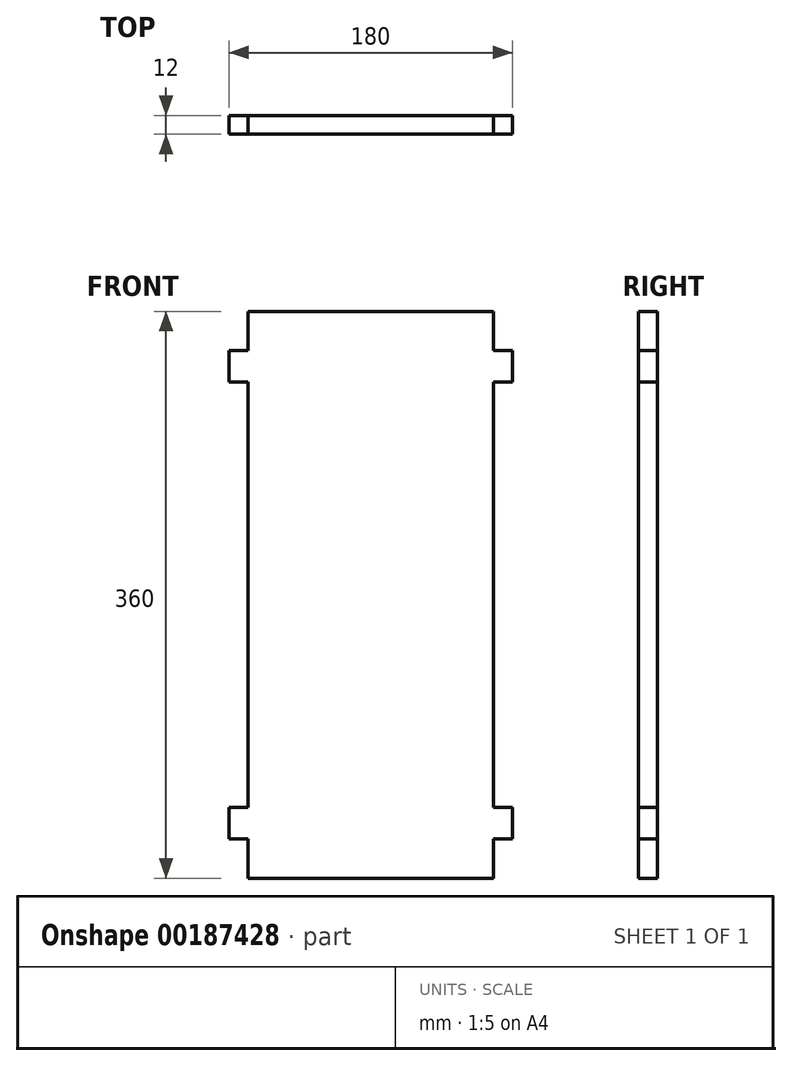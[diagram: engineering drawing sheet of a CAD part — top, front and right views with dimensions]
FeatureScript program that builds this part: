
annotation { "Feature Type Name" : "Feature", "Feature Type Description" : "" }
export const myFeature = defineFeature(function(context is Context, id is Id, definition is map)
    precondition{}
    {
        {
            var Q0;
            Q0=qCreatedBy(makeId("Front.planeOp"),FACE);
            var sketch = newSketch(context, id + "F0", { "sketchPlane" : qUnion([Q0])});
            skLineSegment(sketch, "E0.bottom", {"start": v(90, 180) * mm, "end": v(-90, 180) * mm});
            skLineSegment(sketch, "E0.top", {"start": v(90, -180) * mm, "end": v(-90, -180) * mm});
            skLineSegment(sketch, "E0.left", {"start": v(90, 180) * mm, "end": v(90, -180) * mm});
            skLineSegment(sketch, "E0.right", {"start": v(-90, 180) * mm, "end": v(-90, -180) * mm});
            skPoint(sketch, "E0.middle", {"position": v(0, 0) * mm});
            skLineSegment(sketch, "E1.bottom", {"start": v(-78, -135) * mm, "end": v(-102, -135) * mm});
            skLineSegment(sketch, "E1.top", {"start": v(-78, -155) * mm, "end": v(-102, -155) * mm});
            skLineSegment(sketch, "E1.left", {"start": v(-78, -135) * mm, "end": v(-78, -155) * mm});
            skLineSegment(sketch, "E1.right", {"start": v(-102, -135) * mm, "end": v(-102, -155) * mm});
            skPoint(sketch, "E1.middle", {"position": v(-90, -145) * mm});
            skLineSegment(sketch, "E2.MirrorCS", {"start": v(102, -135) * mm, "end": v(102, -155) * mm});
            skLineSegment(sketch, "E3.MirrorCS", {"start": v(78, -135) * mm, "end": v(102, -135) * mm});
            skLineSegment(sketch, "E4.MirrorCS", {"start": v(78, -155) * mm, "end": v(102, -155) * mm});
            skLineSegment(sketch, "E5.MirrorCS", {"start": v(78, -135) * mm, "end": v(78, -155) * mm});
            skPoint(sketch, "E6.MirrorP", {"position": v(90, -145) * mm});
            skLineSegment(sketch, "E7.bottom", {"start": v(-78, 155) * mm, "end": v(-102, 155) * mm});
            skLineSegment(sketch, "E7.top", {"start": v(-78, 135) * mm, "end": v(-102, 135) * mm});
            skLineSegment(sketch, "E7.left", {"start": v(-78, 155) * mm, "end": v(-78, 135) * mm});
            skLineSegment(sketch, "E7.right", {"start": v(-102, 155) * mm, "end": v(-102, 135) * mm});
            skPoint(sketch, "E7.middle", {"position": v(-90, 145) * mm});
            skLineSegment(sketch, "E8.MirrorCS", {"start": v(102, 155) * mm, "end": v(102, 135) * mm});
            skLineSegment(sketch, "E9.MirrorCS", {"start": v(78, 155) * mm, "end": v(102, 155) * mm});
            skLineSegment(sketch, "E10.MirrorCS", {"start": v(78, 155) * mm, "end": v(78, 135) * mm});
            skLineSegment(sketch, "E11.MirrorCS", {"start": v(78, 135) * mm, "end": v(102, 135) * mm});
            skPoint(sketch, "E12.MirrorP", {"position": v(90, 145) * mm});
            skSolve(sketch);
        }
        {
            var Q0;
            {var subQ5=sQuery(id+"F0.wireOp",EDGE,"E7.right");Q0=makeQuery(id+"F0.imprint","IMPRINT",FACE,{"disambiguationData":[TD([[makeQuery(id+"F0.imprint","IMPRINT",EDGE,{"derivedFrom":subQ5}),1.0]])]});}
            var Q1;
            {var subQ5=sQuery(id+"F0.wireOp",EDGE,"E1.right");Q1=makeQuery(id+"F0.imprint","IMPRINT",FACE,{"disambiguationData":[TD([[makeQuery(id+"F0.imprint","IMPRINT",EDGE,{"derivedFrom":subQ5}),1.0]])]});}
            var Q2;
            {var subQ0=sQuery(id+"F0.wireOp",EDGE,"E2.MirrorCS");Q2=makeQuery(id+"F0.imprint","IMPRINT",FACE,{"disambiguationData":[TD([[makeQuery(id+"F0.imprint","IMPRINT",EDGE,{"derivedFrom":subQ0}),-1.0]])]});}
            var Q3;
            {var subQ5=sQuery(id+"F0.wireOp",EDGE,"E8.MirrorCS");Q3=makeQuery(id+"F0.imprint","IMPRINT",FACE,{"disambiguationData":[TD([[makeQuery(id+"F0.imprint","IMPRINT",EDGE,{"derivedFrom":subQ5}),-1.0]])]});}
            var Q4;
            {var subQ5=sQuery(id+"F0.wireOp",EDGE,"E7.left");Q4=makeQuery(id+"F0.imprint","IMPRINT",FACE,{"disambiguationData":[TD([[makeQuery(id+"F0.imprint","IMPRINT",EDGE,{"derivedFrom":subQ5}),-1.0]])]});}
            var Q5;
            {var subQ5=sQuery(id+"F0.wireOp",EDGE,"E1.left");Q5=makeQuery(id+"F0.imprint","IMPRINT",FACE,{"disambiguationData":[TD([[makeQuery(id+"F0.imprint","IMPRINT",EDGE,{"derivedFrom":subQ5}),-1.0]])]});}
            var Q6;
            {var subQ0=sQuery(id+"F0.wireOp",EDGE,"E5.MirrorCS");Q6=makeQuery(id+"F0.imprint","IMPRINT",FACE,{"disambiguationData":[TD([[makeQuery(id+"F0.imprint","IMPRINT",EDGE,{"derivedFrom":subQ0}),1.0]])]});}
            var Q7;
            {var subQ5=sQuery(id+"F0.wireOp",EDGE,"E10.MirrorCS");Q7=makeQuery(id+"F0.imprint","IMPRINT",FACE,{"disambiguationData":[TD([[makeQuery(id+"F0.imprint","IMPRINT",EDGE,{"derivedFrom":subQ5}),1.0]])]});}
            var Q8;
            {var subQ17=sQuery(id+"F0.wireOp",EDGE,"E0.bottom");Q8=makeQuery(id+"F0.imprint","IMPRINT",FACE,{"disambiguationData":[TD([[makeQuery(id+"F0.imprint","IMPRINT",EDGE,{"derivedFrom":subQ17}),1.0]])]});}
            extrude(context, id + "F1", {"entities" : qUnion([Q0, Q1, Q2, Q3, Q4, Q5, Q6, Q7, Q8]), "depth" : 12 * mm});
        }
        {
            var Q0;
            {var subQ0=sQuery(id+"F0.wireOp",EDGE,"E0.left");Q0=makeQuery(id+"F1.opExtrude","SWEPT_FACE",FACE,{"disambiguationData":[OSD([subQ0]),TDD([makeQuery(id+"F0.imprint","IMPRINT",EDGE,{"disambiguationData":[TD([[makeQuery(id+"F0.imprint","INTERSECT",VERTEX,{"derivedFrom":[sQuery(id+"F0.wireOp",EDGE,"E0.bottom"),subQ0]}),-1.0]])],"derivedFrom":subQ0})])]});}
            var Q1;
            Q1=makeQuery(id+"F1.opExtrude","SWEPT_FACE",FACE,{"disambiguationData":[OSD([sQuery(id+"F0.wireOp",EDGE,"E8.MirrorCS")])]});
            var Q2;
            {var subQ0=sQuery(id+"F0.wireOp",EDGE,"E0.left");Q2=makeQuery(id+"F1.opExtrude","SWEPT_FACE",FACE,{"disambiguationData":[OSD([subQ0]),TDD([makeQuery(id+"F0.imprint","IMPRINT",EDGE,{"disambiguationData":[TD([[makeQuery(id+"F0.imprint","INTERSECT",VERTEX,{"derivedFrom":[sQuery(id+"F0.wireOp",EDGE,"E3.MirrorCS"),subQ0]}),1.0]])],"derivedFrom":subQ0})])]});}
            var Q3;
            Q3=makeQuery(id+"F1.opExtrude","SWEPT_FACE",FACE,{"disambiguationData":[OSD([sQuery(id+"F0.wireOp",EDGE,"E2.MirrorCS")])]});
            var Q4;
            {var subQ0=sQuery(id+"F0.wireOp",EDGE,"E0.left");Q4=makeQuery(id+"F1.opExtrude","SWEPT_FACE",FACE,{"disambiguationData":[OSD([subQ0]),TDD([makeQuery(id+"F0.imprint","IMPRINT",EDGE,{"disambiguationData":[TD([[makeQuery(id+"F0.imprint","INTERSECT",VERTEX,{"derivedFrom":[sQuery(id+"F0.wireOp",EDGE,"E0.top"),subQ0]}),1.0]])],"derivedFrom":subQ0})])]});}
            var Q5;
            {var subQ0=sQuery(id+"F0.wireOp",EDGE,"E0.right");Q5=makeQuery(id+"F1.opExtrude","SWEPT_FACE",FACE,{"disambiguationData":[OSD([subQ0]),TDD([makeQuery(id+"F0.imprint","IMPRINT",EDGE,{"disambiguationData":[TD([[makeQuery(id+"F0.imprint","INTERSECT",VERTEX,{"derivedFrom":[sQuery(id+"F0.wireOp",EDGE,"E0.top"),subQ0]}),1.0]])],"derivedFrom":subQ0})])]});}
            var Q6;
            Q6=makeQuery(id+"F1.opExtrude","SWEPT_FACE",FACE,{"disambiguationData":[OSD([sQuery(id+"F0.wireOp",EDGE,"E1.right")])]});
            var Q7;
            {var subQ0=sQuery(id+"F0.wireOp",EDGE,"E0.right");Q7=makeQuery(id+"F1.opExtrude","SWEPT_FACE",FACE,{"disambiguationData":[OSD([subQ0]),TDD([makeQuery(id+"F0.imprint","IMPRINT",EDGE,{"disambiguationData":[TD([[makeQuery(id+"F0.imprint","INTERSECT",VERTEX,{"derivedFrom":[subQ0,sQuery(id+"F0.wireOp",EDGE,"E7.top")]}),-1.0]])],"derivedFrom":subQ0})])]});}
            var Q8;
            {var subQ0=sQuery(id+"F0.wireOp",EDGE,"E0.right");Q8=makeQuery(id+"F1.opExtrude","SWEPT_FACE",FACE,{"disambiguationData":[OSD([subQ0]),TDD([makeQuery(id+"F0.imprint","IMPRINT",EDGE,{"disambiguationData":[TD([[makeQuery(id+"F0.imprint","INTERSECT",VERTEX,{"derivedFrom":[sQuery(id+"F0.wireOp",EDGE,"E0.bottom"),subQ0]}),-1.0]])],"derivedFrom":subQ0})])]});}
            var Q9;
            Q9=makeQuery(id+"F1.opExtrude","SWEPT_FACE",FACE,{"disambiguationData":[OSD([sQuery(id+"F0.wireOp",EDGE,"E7.right")])]});
            extrude(context, id + "F2", {"entities" : qUnion([Q0, Q1, Q2, Q3, Q4, Q5, Q6, Q7, Q8, Q9]), "operationType" : NewBodyOperationType.REMOVE, "endBound" : BoundingType.SYMMETRIC, "depth" : 4 * mm});
        }
        {
            var Q0;
            {var subQ0=sQuery(id+"F0.wireOp",EDGE,"E0.left");Q0=makeQuery(id+"F2.boolean.opBoolean","COPY",FACE,{"derivedFrom":makeQuery(id+"F2.opExtrude","CAP_FACE",FACE,{"disambiguationData":[OSD([subQ0]),TDD([makeQuery(id+"F1.opExtrude","SWEPT_FACE",FACE,{"disambiguationData":[OSD([subQ0]),TDD([makeQuery(id+"F0.imprint","IMPRINT",EDGE,{"disambiguationData":[TD([[makeQuery(id+"F0.imprint","INTERSECT",VERTEX,{"derivedFrom":[sQuery(id+"F0.wireOp",EDGE,"E0.bottom"),subQ0]}),-1.0]])],"derivedFrom":subQ0})])]})])],"isStart":true})});}
            var Q1;
            Q1=makeQuery(id+"F2.boolean.opBoolean","COPY",FACE,{"derivedFrom":makeQuery(id+"F2.opExtrude","CAP_FACE",FACE,{"disambiguationData":[OSD([sQuery(id+"F0.wireOp",EDGE,"E8.MirrorCS")])],"isStart":true})});
            var Q2;
            {var subQ0=sQuery(id+"F0.wireOp",EDGE,"E0.left");Q2=makeQuery(id+"F2.boolean.opBoolean","COPY",FACE,{"derivedFrom":makeQuery(id+"F2.opExtrude","CAP_FACE",FACE,{"disambiguationData":[OSD([subQ0]),TDD([makeQuery(id+"F1.opExtrude","SWEPT_FACE",FACE,{"disambiguationData":[OSD([subQ0]),TDD([makeQuery(id+"F0.imprint","IMPRINT",EDGE,{"disambiguationData":[TD([[makeQuery(id+"F0.imprint","INTERSECT",VERTEX,{"derivedFrom":[sQuery(id+"F0.wireOp",EDGE,"E3.MirrorCS"),subQ0]}),1.0]])],"derivedFrom":subQ0})])]})])],"isStart":true})});}
            var Q3;
            Q3=makeQuery(id+"F2.boolean.opBoolean","COPY",FACE,{"derivedFrom":makeQuery(id+"F2.opExtrude","CAP_FACE",FACE,{"disambiguationData":[OSD([sQuery(id+"F0.wireOp",EDGE,"E2.MirrorCS")])],"isStart":true})});
            var Q4;
            {var subQ0=sQuery(id+"F0.wireOp",EDGE,"E0.left");Q4=makeQuery(id+"F2.boolean.opBoolean","COPY",FACE,{"derivedFrom":makeQuery(id+"F2.opExtrude","CAP_FACE",FACE,{"disambiguationData":[OSD([subQ0]),TDD([makeQuery(id+"F1.opExtrude","SWEPT_FACE",FACE,{"disambiguationData":[OSD([subQ0]),TDD([makeQuery(id+"F0.imprint","IMPRINT",EDGE,{"disambiguationData":[TD([[makeQuery(id+"F0.imprint","INTERSECT",VERTEX,{"derivedFrom":[sQuery(id+"F0.wireOp",EDGE,"E0.top"),subQ0]}),1.0]])],"derivedFrom":subQ0})])]})])],"isStart":true})});}
            extrude(context, id + "F3", {"entities" : qUnion([Q0, Q1, Q2, Q3, Q4]), "operationType" : NewBodyOperationType.REMOVE, "oppositeDirection" : true, "depth" : 10 * mm, "offsetDistance" : 25 * mm});
        }
        {
            var Q0;
            {var subQ0=sQuery(id+"F0.wireOp",EDGE,"E0.right");Q0=makeQuery(id+"F2.boolean.opBoolean","COPY",FACE,{"derivedFrom":makeQuery(id+"F2.opExtrude","CAP_FACE",FACE,{"disambiguationData":[OSD([subQ0]),TDD([makeQuery(id+"F1.opExtrude","SWEPT_FACE",FACE,{"disambiguationData":[OSD([subQ0]),TDD([makeQuery(id+"F0.imprint","IMPRINT",EDGE,{"disambiguationData":[TD([[makeQuery(id+"F0.imprint","INTERSECT",VERTEX,{"derivedFrom":[sQuery(id+"F0.wireOp",EDGE,"E0.bottom"),subQ0]}),-1.0]])],"derivedFrom":subQ0})])]})])],"isStart":false})});}
            var Q1;
            Q1=makeQuery(id+"F2.boolean.opBoolean","COPY",FACE,{"derivedFrom":makeQuery(id+"F2.opExtrude","CAP_FACE",FACE,{"disambiguationData":[OSD([sQuery(id+"F0.wireOp",EDGE,"E7.right")])],"isStart":false})});
            var Q2;
            {var subQ0=sQuery(id+"F0.wireOp",EDGE,"E0.right");Q2=makeQuery(id+"F2.boolean.opBoolean","COPY",FACE,{"derivedFrom":makeQuery(id+"F2.opExtrude","CAP_FACE",FACE,{"disambiguationData":[OSD([subQ0]),TDD([makeQuery(id+"F1.opExtrude","SWEPT_FACE",FACE,{"disambiguationData":[OSD([subQ0]),TDD([makeQuery(id+"F0.imprint","IMPRINT",EDGE,{"disambiguationData":[TD([[makeQuery(id+"F0.imprint","INTERSECT",VERTEX,{"derivedFrom":[subQ0,sQuery(id+"F0.wireOp",EDGE,"E7.top")]}),-1.0]])],"derivedFrom":subQ0})])]})])],"isStart":false})});}
            var Q3;
            Q3=makeQuery(id+"F2.boolean.opBoolean","COPY",FACE,{"derivedFrom":makeQuery(id+"F2.opExtrude","CAP_FACE",FACE,{"disambiguationData":[OSD([sQuery(id+"F0.wireOp",EDGE,"E1.right")])],"isStart":false})});
            var Q4;
            {var subQ0=sQuery(id+"F0.wireOp",EDGE,"E0.right");Q4=makeQuery(id+"F2.boolean.opBoolean","COPY",FACE,{"derivedFrom":makeQuery(id+"F2.opExtrude","CAP_FACE",FACE,{"disambiguationData":[OSD([subQ0]),TDD([makeQuery(id+"F1.opExtrude","SWEPT_FACE",FACE,{"disambiguationData":[OSD([subQ0]),TDD([makeQuery(id+"F0.imprint","IMPRINT",EDGE,{"disambiguationData":[TD([[makeQuery(id+"F0.imprint","INTERSECT",VERTEX,{"derivedFrom":[sQuery(id+"F0.wireOp",EDGE,"E0.top"),subQ0]}),1.0]])],"derivedFrom":subQ0})])]})])],"isStart":false})});}
            extrude(context, id + "F4", {"entities" : qUnion([Q0, Q1, Q2, Q3, Q4]), "operationType" : NewBodyOperationType.REMOVE, "oppositeDirection" : true, "depth" : 10 * mm, "offsetDistance" : 25 * mm});
        }
    });
